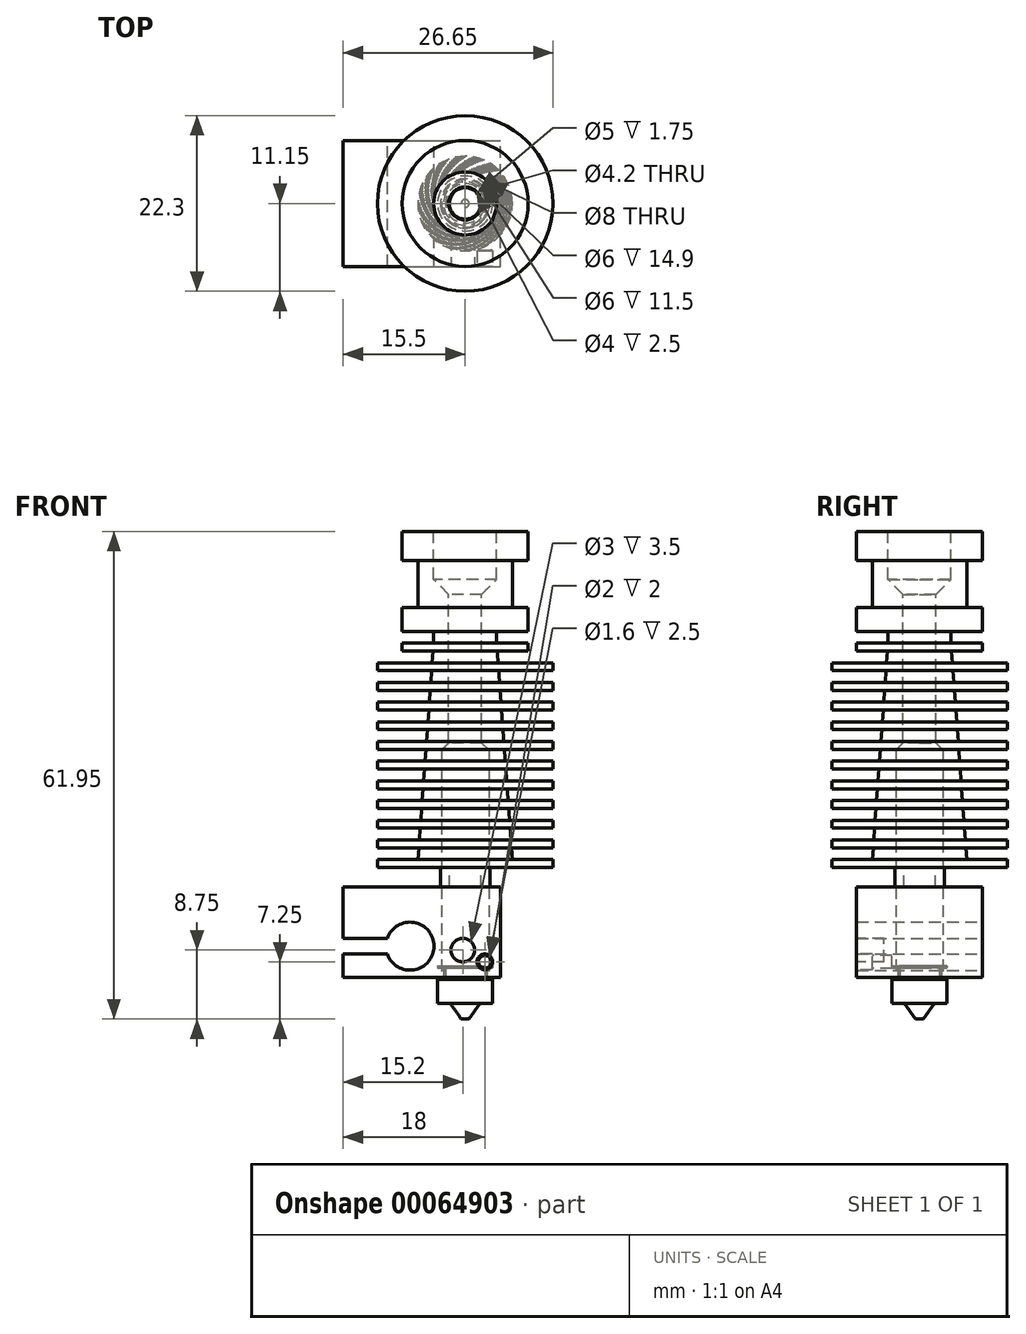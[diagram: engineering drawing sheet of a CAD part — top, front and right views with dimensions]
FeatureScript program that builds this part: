
annotation { "Feature Type Name" : "Feature", "Feature Type Description" : "" }
export const myFeature = defineFeature(function(context is Context, id is Id, definition is map)
    precondition{}
    {
        {
            var Q0;
            Q0=qCreatedBy(makeId("Top.planeOp"),FACE);
            var sketch = newSketch(context, id + "F0", { "sketchPlane" : qUnion([Q0])});
            skCircle(sketch, "E0", {"center": v(0, 0) * mm, "radius": 8 * mm});
            skSolve(sketch);
        }
        {
            var Q0;
            Q0=makeQuery(id+"F0.imprint","IMPRINT",FACE,{"disambiguationData":[TD([[makeQuery(id+"F0.imprint","IMPRINT",EDGE,{"derivedFrom":sQuery(id+"F0.wireOp",EDGE,"E0")}),1.0]])]});
            var Q1;
            Q1=sQuery(id+"F0.wireOp",EDGE,"E0");
            extrude(context, id + "F1", {"entities" : qUnion([Q0]), "surfaceEntities" : qUnion([Q1]), "oppositeDirection" : true, "depth" : 3.7 * mm});
        }
        {
            var Q0;
            Q0=makeQuery(id+"F1.opExtrude","CAP_FACE",FACE,{"disambiguationData":[OSD([sQuery(id+"F0.wireOp",EDGE,"E0")])],"isStart":false});
            var sketch = newSketch(context, id + "F2", { "sketchPlane" : qUnion([Q0])});
            skCircle(sketch, "E1", {"center": v(0, 0) * mm, "radius": 6 * mm});
            skSolve(sketch);
        }
        {
            var Q0;
            Q0=makeQuery(id+"F2.imprint","IMPRINT",FACE,{"disambiguationData":[TD([[makeQuery(id+"F2.imprint","IMPRINT",EDGE,{"derivedFrom":sQuery(id+"F2.wireOp",EDGE,"E1")}),1.0]])]});
            var Q1;
            Q1=sQuery(id+"F2.wireOp",EDGE,"E1");
            extrude(context, id + "F3", {"entities" : qUnion([Q0]), "operationType" : NewBodyOperationType.ADD, "surfaceEntities" : qUnion([Q1]), "depth" : 6 * mm});
        }
        {
            var Q0;
            Q0=makeQuery(id+"F3.opExtrude","CAP_FACE",FACE,{"disambiguationData":[OSD([sQuery(id+"F2.wireOp",EDGE,"E1")])],"isStart":false});
            var sketch = newSketch(context, id + "F4", { "sketchPlane" : qUnion([Q0])});
            skCircle(sketch, "E2", {"center": v(0, 0) * mm, "radius": 8 * mm});
            skSolve(sketch);
        }
        {
            var Q0;
            Q0=qSketchRegion(id+"F4",true);
            extrude(context, id + "F5", {"entities" : qUnion([Q0]), "operationType" : NewBodyOperationType.ADD, "depth" : 3 * mm});
        }
        {
            var Q0;
            Q0=qCreatedBy(makeId("Front.planeOp"),FACE);
            var sketch = newSketch(context, id + "F6", { "sketchPlane" : qUnion([Q0])});
            skLineSegment(sketch, "E3", {"start": v(0, 0) * mm, "end": v(0, -12.7) * mm});
            skLineSegment(sketch, "E4.bottom", {"start": v(0, -12.7) * mm, "end": v(4, -12.7) * mm});
            skLineSegment(sketch, "E4.top", {"start": v(0, -14.2) * mm, "end": v(4, -14.2) * mm});
            skLineSegment(sketch, "E4.left", {"start": v(0, -12.7) * mm, "end": v(0, -14.2) * mm});
            skLineSegment(sketch, "E4.right", {"start": v(4, -12.7) * mm, "end": v(4, -14.2) * mm});
            skLineSegment(sketch, "E5.bottom", {"start": v(0, -14.2) * mm, "end": v(8, -14.2) * mm});
            skLineSegment(sketch, "E5.top", {"start": v(0, -15.2) * mm, "end": v(8, -15.2) * mm});
            skLineSegment(sketch, "E5.left", {"start": v(0, -14.2) * mm, "end": v(0, -15.2) * mm});
            skLineSegment(sketch, "E5.right", {"start": v(8, -14.2) * mm, "end": v(8, -15.2) * mm});
            skLineSegment(sketch, "E6", {"start": v(0, -15.2) * mm, "end": v(0, -16.7) * mm});
            skLineSegment(sketch, "E7.bottom", {"start": v(0, -16.7) * mm, "end": v(11.15, -16.7) * mm});
            skLineSegment(sketch, "E7.top", {"start": v(0, -17.7) * mm, "end": v(11.15, -17.7) * mm});
            skLineSegment(sketch, "E7.left", {"start": v(0, -16.7) * mm, "end": v(0, -17.7) * mm});
            skLineSegment(sketch, "E7.right", {"start": v(11.15, -16.7) * mm, "end": v(11.15, -17.7) * mm});
            skLineSegment(sketch, "E8.1.0.0", {"start": v(0, -20.2) * mm, "end": v(11.15, -20.2) * mm});
            skLineSegment(sketch, "E8.1.0.1", {"start": v(0, -19.2) * mm, "end": v(11.15, -19.2) * mm});
            skLineSegment(sketch, "E8.1.0.2", {"start": v(0, -19.2) * mm, "end": v(0, -20.2) * mm});
            skLineSegment(sketch, "E8.1.0.3", {"start": v(11.15, -19.2) * mm, "end": v(11.15, -20.2) * mm});
            skLineSegment(sketch, "E8.2.0.0", {"start": v(0, -22.7) * mm, "end": v(11.15, -22.7) * mm});
            skLineSegment(sketch, "E8.2.0.1", {"start": v(0, -21.7) * mm, "end": v(11.15, -21.7) * mm});
            skLineSegment(sketch, "E8.2.0.2", {"start": v(0, -21.7) * mm, "end": v(0, -22.7) * mm});
            skLineSegment(sketch, "E8.2.0.3", {"start": v(11.15, -21.7) * mm, "end": v(11.15, -22.7) * mm});
            skLineSegment(sketch, "E8.3.0.0", {"start": v(0, -25.2) * mm, "end": v(11.15, -25.2) * mm});
            skLineSegment(sketch, "E8.3.0.1", {"start": v(0, -24.2) * mm, "end": v(11.15, -24.2) * mm});
            skLineSegment(sketch, "E8.3.0.2", {"start": v(0, -24.2) * mm, "end": v(0, -25.2) * mm});
            skLineSegment(sketch, "E8.3.0.3", {"start": v(11.15, -24.2) * mm, "end": v(11.15, -25.2) * mm});
            skLineSegment(sketch, "E8.4.0.0", {"start": v(0, -27.7) * mm, "end": v(11.15, -27.7) * mm});
            skLineSegment(sketch, "E8.4.0.1", {"start": v(0, -26.7) * mm, "end": v(11.15, -26.7) * mm});
            skLineSegment(sketch, "E8.4.0.2", {"start": v(0, -26.7) * mm, "end": v(0, -27.7) * mm});
            skLineSegment(sketch, "E8.4.0.3", {"start": v(11.15, -26.7) * mm, "end": v(11.15, -27.7) * mm});
            skLineSegment(sketch, "E8.5.0.0", {"start": v(0, -30.2) * mm, "end": v(11.15, -30.2) * mm});
            skLineSegment(sketch, "E8.5.0.1", {"start": v(0, -29.2) * mm, "end": v(11.15, -29.2) * mm});
            skLineSegment(sketch, "E8.5.0.2", {"start": v(0, -29.2) * mm, "end": v(0, -30.2) * mm});
            skLineSegment(sketch, "E8.5.0.3", {"start": v(11.15, -29.2) * mm, "end": v(11.15, -30.2) * mm});
            skLineSegment(sketch, "E8.6.0.0", {"start": v(0, -32.7) * mm, "end": v(11.15, -32.7) * mm});
            skLineSegment(sketch, "E8.6.0.1", {"start": v(0, -31.7) * mm, "end": v(11.15, -31.7) * mm});
            skLineSegment(sketch, "E8.6.0.2", {"start": v(0, -31.7) * mm, "end": v(0, -32.7) * mm});
            skLineSegment(sketch, "E8.6.0.3", {"start": v(11.15, -31.7) * mm, "end": v(11.15, -32.7) * mm});
            skLineSegment(sketch, "E8.7.0.0", {"start": v(0, -35.2) * mm, "end": v(11.15, -35.2) * mm});
            skLineSegment(sketch, "E8.7.0.1", {"start": v(0, -34.2) * mm, "end": v(11.15, -34.2) * mm});
            skLineSegment(sketch, "E8.7.0.2", {"start": v(0, -34.2) * mm, "end": v(0, -35.2) * mm});
            skLineSegment(sketch, "E8.7.0.3", {"start": v(11.15, -34.2) * mm, "end": v(11.15, -35.2) * mm});
            skLineSegment(sketch, "E8.8.0.0", {"start": v(0, -37.7) * mm, "end": v(11.15, -37.7) * mm});
            skLineSegment(sketch, "E8.8.0.1", {"start": v(0, -36.7) * mm, "end": v(11.15, -36.7) * mm});
            skLineSegment(sketch, "E8.8.0.2", {"start": v(0, -36.7) * mm, "end": v(0, -37.7) * mm});
            skLineSegment(sketch, "E8.8.0.3", {"start": v(11.15, -36.7) * mm, "end": v(11.15, -37.7) * mm});
            skLineSegment(sketch, "E8.9.0.0", {"start": v(0, -40.2) * mm, "end": v(11.15, -40.2) * mm});
            skLineSegment(sketch, "E8.9.0.1", {"start": v(0, -39.2) * mm, "end": v(11.15, -39.2) * mm});
            skLineSegment(sketch, "E8.9.0.2", {"start": v(0, -39.2) * mm, "end": v(0, -40.2) * mm});
            skLineSegment(sketch, "E8.9.0.3", {"start": v(11.15, -39.2) * mm, "end": v(11.15, -40.2) * mm});
            skLineSegment(sketch, "E8.10.0.0", {"start": v(0, -42.7) * mm, "end": v(11.15, -42.7) * mm});
            skLineSegment(sketch, "E8.10.0.1", {"start": v(0, -41.7) * mm, "end": v(11.15, -41.7) * mm});
            skLineSegment(sketch, "E8.10.0.2", {"start": v(0, -41.7) * mm, "end": v(0, -42.7) * mm});
            skLineSegment(sketch, "E8.10.0.3", {"start": v(11.15, -41.7) * mm, "end": v(11.15, -42.7) * mm});
            skLineSegment(sketch, "E8.direction1", {"start": v(0, -17.7) * mm, "end": v(0, -20.2) * mm, "construction": true});
            skLineSegment(sketch, "E9", {"start": v(0, -41.7) * mm, "end": v(6, -41.7) * mm});
            skLineSegment(sketch, "E10", {"start": v(4.07, -15.2) * mm, "end": v(4.18, -16.7) * mm});
            skLineSegment(sketch, "E11.trimOffspring", {"start": v(4.25, -17.7) * mm, "end": v(4.36, -19.2) * mm});
            skLineSegment(sketch, "E12.trimOffspring", {"start": v(4.44, -20.2) * mm, "end": v(4.55, -21.7) * mm});
            skLineSegment(sketch, "E13.trimOffspring", {"start": v(4.62, -22.7) * mm, "end": v(4.73, -24.2) * mm});
            skLineSegment(sketch, "E14.trimOffspring", {"start": v(4.8, -25.2) * mm, "end": v(4.9, -26.7) * mm});
            skLineSegment(sketch, "E15.trimOffspring", {"start": v(4.98, -27.7) * mm, "end": v(5.1, -29.2) * mm});
            skLineSegment(sketch, "E16.trimOffspring", {"start": v(5.16, -30.2) * mm, "end": v(5.27, -31.7) * mm});
            skLineSegment(sketch, "E17.trimOffspring", {"start": v(5.35, -32.7) * mm, "end": v(5.45, -34.2) * mm});
            skLineSegment(sketch, "E18.trimOffspring", {"start": v(5.53, -35.2) * mm, "end": v(5.64, -36.7) * mm});
            skLineSegment(sketch, "E19.trimOffspring", {"start": v(5.7, -37.7) * mm, "end": v(5.82, -39.2) * mm});
            skLineSegment(sketch, "E20.trimOffspring", {"start": v(5.9, -40.2) * mm, "end": v(6, -41.7) * mm});
            skLineSegment(sketch, "E21", {"start": v(0, -17.7) * mm, "end": v(0, -19.2) * mm});
            skLineSegment(sketch, "E22", {"start": v(0, -20.2) * mm, "end": v(0, -21.7) * mm});
            skLineSegment(sketch, "E23", {"start": v(0, -22.7) * mm, "end": v(0, -24.2) * mm});
            skLineSegment(sketch, "E24", {"start": v(0, -25.2) * mm, "end": v(0, -26.7) * mm});
            skLineSegment(sketch, "E25", {"start": v(0, -27.7) * mm, "end": v(0, -29.2) * mm});
            skLineSegment(sketch, "E26", {"start": v(0, -30.2) * mm, "end": v(0, -31.7) * mm});
            skLineSegment(sketch, "E27", {"start": v(0, -32.7) * mm, "end": v(0, -34.2) * mm});
            skLineSegment(sketch, "E28", {"start": v(0, -35.2) * mm, "end": v(0, -36.7) * mm});
            skLineSegment(sketch, "E29", {"start": v(0, -37.7) * mm, "end": v(0, -39.2) * mm});
            skLineSegment(sketch, "E30", {"start": v(0, -40.2) * mm, "end": v(0, -41.7) * mm});
            skLineSegment(sketch, "E31.right", {"start": v(3, -42.7) * mm, "end": v(3, -45.2) * mm});
            skLineSegment(sketch, "E32", {"start": v(3, -45.2) * mm, "end": v(2, -45.2) * mm});
            skLineSegment(sketch, "E33", {"start": v(2, -45.2) * mm, "end": v(2, -42.7) * mm});
            skLineSegment(sketch, "E34.bottom", {"start": v(2, -45.2) * mm, "end": v(3, -45.2) * mm});
            skLineSegment(sketch, "E34.top", {"start": v(2, -47.3) * mm, "end": v(3, -47.3) * mm});
            skLineSegment(sketch, "E34.left", {"start": v(2, -45.2) * mm, "end": v(2, -47.3) * mm});
            skLineSegment(sketch, "E34.right", {"start": v(3, -45.2) * mm, "end": v(3, -47.3) * mm});
            skLineSegment(sketch, "E35.bottom", {"start": v(3, -47.3) * mm, "end": v(3.75, -47.3) * mm});
            skLineSegment(sketch, "E35.top", {"start": v(3, -46.56) * mm, "end": v(3.75, -46.56) * mm});
            skLineSegment(sketch, "E35.left", {"start": v(3, -47.3) * mm, "end": v(3, -46.56) * mm});
            skLineSegment(sketch, "E35.right", {"start": v(3.75, -47.3) * mm, "end": v(3.75, -46.56) * mm});
            skLineSegment(sketch, "E36.bottom", {"start": v(2, -42.7) * mm, "end": v(3, -42.7) * mm});
            skLineSegment(sketch, "E36.top", {"start": v(2, -41.7) * mm, "end": v(3, -41.7) * mm});
            skLineSegment(sketch, "E36.left", {"start": v(2, -42.7) * mm, "end": v(2, -41.7) * mm});
            skLineSegment(sketch, "E36.right", {"start": v(3, -42.7) * mm, "end": v(3, -41.7) * mm});
            skSolve(sketch);
        }
        {
            var Q0;
            Q0=qSketchRegion(id+"F6",true);
            var Q1;
            {var subQ0=sQuery(id+"F6.wireOp",EDGE,"E31.right");Q1=makeQuery(id+"F6.imprint","IMPRINT",FACE,{"disambiguationData":[TD([[makeQuery(id+"F6.imprint","IMPRINT",EDGE,{"derivedFrom":subQ0}),-1.0]])]});}
            var Q2;
            Q2=makeQuery(id+"F6.imprint","IMPRINT",FACE,{"disambiguationData":[TD([[makeQuery(id+"F6.imprint","IMPRINT",EDGE,{"derivedFrom":sQuery(id+"F6.wireOp",EDGE,"E34.bottom")}),-1.0]])]});
            var Q3;
            Q3=makeQuery(id+"F6.imprint","IMPRINT",FACE,{"disambiguationData":[TD([[makeQuery(id+"F6.imprint","IMPRINT",EDGE,{"derivedFrom":sQuery(id+"F6.wireOp",EDGE,"E36.bottom")}),1.0]])]});
            var Q4;
            Q4=makeQuery(id+"F6.imprint","IMPRINT",FACE,{"disambiguationData":[TD([[makeQuery(id+"F6.imprint","IMPRINT",EDGE,{"derivedFrom":sQuery(id+"F6.wireOp",EDGE,"E31.right")}),-1.0]])]});
            var Q5;
            Q5=makeQuery(id+"F6.imprint","IMPRINT",FACE,{"disambiguationData":[TD([[makeQuery(id+"F6.imprint","IMPRINT",EDGE,{"derivedFrom":sQuery(id+"F6.wireOp",EDGE,"E34.bottom")}),-1.0]])]});
            var Q6;
            Q6=sQuery(id+"F6.wireOp",EDGE,"E3");
            revolve(context, id + "F7", {"operationType" : NewBodyOperationType.ADD, "entities" : qUnion([Q0, Q1, Q2, Q3, Q4, Q5]), "axis" : qUnion([Q6]), "revolveType" : RevolveType.FULL});
        }
        {
            var Q0;
            Q0=makeQuery(id+"F1.opExtrude","CAP_FACE",FACE,{"disambiguationData":[OSD([sQuery(id+"F0.wireOp",EDGE,"E0")])],"isStart":true});
            var sketch = newSketch(context, id + "F8", { "sketchPlane" : qUnion([Q0])});
            skCircle(sketch, "E37", {"center": v(0, 0) * mm, "radius": 2.1 * mm});
            skSolve(sketch);
        }
        {
            var Q0;
            Q0=qSketchRegion(id+"F8",true);
            extrude(context, id + "F9", {"entities" : qUnion([Q0]), "operationType" : NewBodyOperationType.REMOVE, "oppositeDirection" : true, "depth" : 42.7 * mm});
        }
        {
            var Q0;
            Q0=makeQuery(id+"F1.opExtrude","CAP_FACE",FACE,{"disambiguationData":[OSD([sQuery(id+"F0.wireOp",EDGE,"E0")])],"isStart":true});
            var sketch = newSketch(context, id + "F10", { "sketchPlane" : qUnion([Q0])});
            skCircle(sketch, "E38", {"center": v(0, 0) * mm, "radius": 4 * mm});
            skSolve(sketch);
        }
        {
            var Q0;
            Q0=qSketchRegion(id+"F10",true);
            extrude(context, id + "F11", {"entities" : qUnion([Q0]), "operationType" : NewBodyOperationType.REMOVE, "oppositeDirection" : true, "depth" : 6 * mm});
        }
        {
            var Q0;
            Q0=makeQuery(id+"F11.boolean.opBoolean","INTERSECT",EDGE,{"derivedFrom":[makeQuery(id+"F9.boolean.opBoolean","COPY",FACE,{"derivedFrom":makeQuery(id+"F9.opExtrude","SWEPT_FACE",FACE,{"disambiguationData":[OSD([sQuery(id+"F8.wireOp",EDGE,"E37")])]})}),makeQuery(id+"F11.opExtrude","CAP_FACE",FACE,{"disambiguationData":[OSD([sQuery(id+"F10.wireOp",EDGE,"E38")])],"isStart":false})]});
            chamfer(context, id + "F12", {"entities" : qUnion([Q0]), "width" : 2 * mm, "tangentPropagation" : true});
        }
        {
            var Q0;
            Q0=makeQuery(id+"F7.opRevolve","SWEPT_FACE",FACE,{"disambiguationData":[OSD([sQuery(id+"F6.wireOp",EDGE,"E8.10.0.0")])]});
            var sketch = newSketch(context, id + "F13", { "sketchPlane" : qUnion([Q0])});
            skCircle(sketch, "E39", {"center": v(0, 0) * mm, "radius": 3 * mm});
            skSolve(sketch);
        }
        {
            var Q0;
            Q0=qSketchRegion(id+"F13",true);
            extrude(context, id + "F14", {"entities" : qUnion([Q0]), "operationType" : NewBodyOperationType.REMOVE, "oppositeDirection" : true, "depth" : 14.8 * mm});
        }
        {
            var Q0;
            Q0=makeQuery(id+"F14.boolean.opBoolean","INTERSECT",EDGE,{"derivedFrom":[makeQuery(id+"F9.boolean.opBoolean","COPY",FACE,{"derivedFrom":makeQuery(id+"F9.opExtrude","SWEPT_FACE",FACE,{"disambiguationData":[OSD([sQuery(id+"F8.wireOp",EDGE,"E37")])]})}),makeQuery(id+"F14.opExtrude","CAP_FACE",FACE,{"disambiguationData":[OSD([sQuery(id+"F13.wireOp",EDGE,"E39")])],"isStart":false})]});
            chamfer(context, id + "F15", {"entities" : qUnion([Q0]), "width" : 1 * mm, "tangentPropagation" : true});
        }
        {
            var Q0;
            Q0=qCreatedBy(makeId("Front.planeOp"),FACE);
            var sketch = newSketch(context, id + "F16", { "sketchPlane" : qUnion([Q0])});
            skLineSegment(sketch, "E40.bottom", {"start": v(-15.5, -45.2) * mm, "end": v(4.5, -45.2) * mm});
            skLineSegment(sketch, "E40.top", {"start": v(-15.5, -56.7) * mm, "end": v(4.5, -56.7) * mm});
            skLineSegment(sketch, "E40.left", {"start": v(-15.5, -45.2) * mm, "end": v(-15.5, -51.7) * mm});
            skLineSegment(sketch, "E40.right", {"start": v(4.5, -45.2) * mm, "end": v(4.5, -56.7) * mm});
            skArc(sketch, "E41", {"start": v(-9.88, -53.7) * mm, "mid": v(-3.95, -52.7) * mm, "end": v(-9.88, -51.7) * mm});
            skLineSegment(sketch, "E42.top", {"start": v(-15.5, -51.7) * mm, "end": v(-9.88, -51.7) * mm});
            skLineSegment(sketch, "E43.top", {"start": v(-15.5, -53.7) * mm, "end": v(-9.88, -53.7) * mm});
            skLineSegment(sketch, "E44.trimOffspring", {"start": v(-15.5, -53.7) * mm, "end": v(-15.5, -56.7) * mm});
            skSolve(sketch);
        }
        {
            var Q0;
            Q0=makeQuery(id+"F16.imprint","IMPRINT",FACE,{"disambiguationData":[TD([[makeQuery(id+"F16.imprint","IMPRINT",EDGE,{"derivedFrom":sQuery(id+"F16.wireOp",EDGE,"E40.bottom")}),-1.0]])]});
            var Q1;
            Q1=makeQuery(id+"F16.imprint","IMPRINT",FACE,{"disambiguationData":[TD([[makeQuery(id+"F16.imprint","IMPRINT",EDGE,{"derivedFrom":sQuery(id+"F16.wireOp",EDGE,"hSTLO5rz-Z077-ZaO5-nEVS-phWlFBx8dYmu")}),1.0]])]});
            var Q2;
            Q2=makeQuery(id+"F16.imprint","IMPRINT",FACE,{"disambiguationData":[TD([[makeQuery(id+"F16.imprint","IMPRINT",EDGE,{"derivedFrom":sQuery(id+"F16.wireOp",EDGE,"1ucrc5hz-Jwvr-DOmE-K7qY-mdj6J8iSEPF0")}),1.0]])]});
            extrude(context, id + "F17", {"entities" : qUnion([Q0, Q1, Q2]), "depth" : 16 * mm, "symmetric" : true});
        }
        {
            var Q0;
            Q0=makeQuery(id+"F17.opExtrude","SWEPT_FACE",FACE,{"disambiguationData":[OSD([sQuery(id+"F16.wireOp",EDGE,"E40.top")])]});
            var sketch = newSketch(context, id + "F18", { "sketchPlane" : qUnion([Q0])});
            skCircle(sketch, "E45", {"center": v(0, 0) * mm, "radius": 3 * mm});
            skSolve(sketch);
        }
        {
            var Q0;
            Q0=qSketchRegion(id+"F18",true);
            extrude(context, id + "F19", {"entities" : qUnion([Q0]), "operationType" : NewBodyOperationType.REMOVE, "oppositeDirection" : true, "depth" : 11.5 * mm});
        }
        {
            var Q0;
            Q0=qCreatedBy(makeId("Front.planeOp"),FACE);
            var sketch = newSketch(context, id + "F20", { "sketchPlane" : qUnion([Q0])});
            skLineSegment(sketch, "E46.bottom", {"start": v(0, -56.95) * mm, "end": v(3.5, -56.95) * mm});
            skLineSegment(sketch, "E46.right", {"start": v(3.5, -56.95) * mm, "end": v(3.5, -59.95) * mm});
            skLineSegment(sketch, "E47.top", {"start": v(0, -61.95) * mm, "end": v(0.5, -61.95) * mm});
            skLineSegment(sketch, "E48", {"start": v(0.5, -61.95) * mm, "end": v(1.9, -59.95) * mm});
            skLineSegment(sketch, "E49.trimOffspring", {"start": v(1.9, -59.95) * mm, "end": v(3.5, -59.95) * mm});
            skLineSegment(sketch, "E50", {"start": v(0, -61.95) * mm, "end": v(0, -56.95) * mm});
            skLineSegment(sketch, "E51", {"start": v(0, -56.95) * mm, "end": v(2.5, -56.95) * mm});
            skLineSegment(sketch, "E52", {"start": v(2.5, -56.95) * mm, "end": v(2.5, -55.45) * mm});
            skLineSegment(sketch, "E53", {"start": v(2.5, -55.45) * mm, "end": v(2.75, -55.45) * mm});
            skLineSegment(sketch, "E54", {"start": v(2.75, -55.45) * mm, "end": v(2.75, -56.95) * mm});
            skLineSegment(sketch, "E55.bottom", {"start": v(2.5, -55.45) * mm, "end": v(3.5, -55.45) * mm});
            skLineSegment(sketch, "E55.top", {"start": v(2.5, -55.2) * mm, "end": v(3.5, -55.2) * mm});
            skLineSegment(sketch, "E55.left", {"start": v(2.5, -55.45) * mm, "end": v(2.5, -55.2) * mm});
            skLineSegment(sketch, "E55.right", {"start": v(3.5, -55.45) * mm, "end": v(3.5, -55.2) * mm});
            skSolve(sketch);
        }
        {
            var Q0;
            Q0=qSketchRegion(id+"F20",true);
            var Q1;
            Q1=sQuery(id+"F20.wireOp",EDGE,"E50");
            revolve(context, id + "F21", {"entities" : qUnion([Q0]), "axis" : qUnion([Q1]), "revolveType" : RevolveType.FULL});
        }
        {
            var Q0;
            Q0=makeQuery(id+"F17.opExtrude","CAP_FACE",FACE,{"disambiguationData":[OSD([sQuery(id+"F16.wireOp",EDGE,"E40.bottom"),sQuery(id+"F16.wireOp",EDGE,"E40.top"),sQuery(id+"F16.wireOp",EDGE,"E40.left"),sQuery(id+"F16.wireOp",EDGE,"E40.right"),sQuery(id+"F16.wireOp",EDGE,"E41"),sQuery(id+"F16.wireOp",EDGE,"E42.top"),sQuery(id+"F16.wireOp",EDGE,"E43.top"),sQuery(id+"F16.wireOp",EDGE,"E44.trimOffspring")])],"isStart":false});
            var sketch = newSketch(context, id + "F22", { "sketchPlane" : qUnion([Q0])});
            skCircle(sketch, "E56", {"center": v(-0.3, -53.2) * mm, "radius": 1.5 * mm});
            skCircle(sketch, "E57", {"center": v(2.5, -54.7) * mm, "radius": 1 * mm});
            skCircle(sketch, "E58", {"center": v(2.5, -54.7) * mm, "radius": 0.8 * mm});
            skSolve(sketch);
        }
        {
            var Q0;
            Q0=makeQuery(id+"F22.imprint","IMPRINT",FACE,{"disambiguationData":[TD([[makeQuery(id+"F22.imprint","IMPRINT",EDGE,{"derivedFrom":sQuery(id+"F22.wireOp",EDGE,"E56")}),1.0]])]});
            extrude(context, id + "F23", {"entities" : qUnion([Q0]), "operationType" : NewBodyOperationType.REMOVE, "oppositeDirection" : true, "depth" : 3.5 * mm});
        }
        {
            var Q0;
            Q0=makeQuery(id+"F22.imprint","IMPRINT",FACE,{"disambiguationData":[TD([[makeQuery(id+"F22.imprint","IMPRINT",EDGE,{"derivedFrom":sQuery(id+"F22.wireOp",EDGE,"E57")}),1.0]])]});
            extrude(context, id + "F24", {"entities" : qUnion([Q0]), "operationType" : NewBodyOperationType.REMOVE, "oppositeDirection" : true, "depth" : 2 * mm});
        }
        {
            var Q0;
            Q0=makeQuery(id+"F22.imprint","IMPRINT",FACE,{"disambiguationData":[TD([[makeQuery(id+"F22.imprint","IMPRINT",EDGE,{"derivedFrom":sQuery(id+"F22.wireOp",EDGE,"E58")}),1.0]])]});
            extrude(context, id + "F25", {"entities" : qUnion([Q0]), "operationType" : NewBodyOperationType.REMOVE, "oppositeDirection" : true, "depth" : 4.5 * mm});
        }
        {
            var Q0;
            {var subQ0=sQuery(id+"F6.wireOp",EDGE,"E8.10.0.0");Q0=makeQuery(id+"F7.opRevolve","SWEPT_FACE",FACE,{"disambiguationData":[OSD([subQ0]),TDD([makeQuery(id+"F6.imprint","IMPRINT",EDGE,{"disambiguationData":[TD([[makeQuery(id+"F6.imprint","INTERSECT",VERTEX,{"derivedFrom":[subQ0,sQuery(id+"F6.wireOp",EDGE,"E8.10.0.3")]}),1.0]])],"derivedFrom":subQ0})])]});}
            var sketch = newSketch(context, id + "F26", { "sketchPlane" : qUnion([Q0])});
            skCircle(sketch, "E59", {"center": v(0, 0) * mm, "radius": 3.12 * mm});
            skSolve(sketch);
        }
        {
            var Q0;
            Q0=makeQuery(id+"F26.imprint","IMPRINT",FACE,{"disambiguationData":[TD([[makeQuery(id+"F26.imprint","IMPRINT",EDGE,{"derivedFrom":sQuery(id+"F26.wireOp",EDGE,"E59")}),1.0]])]});
            extrude(context, id + "F27", {"entities" : qUnion([Q0]), "operationType" : NewBodyOperationType.ADD, "depth" : 5 * mm});
        }
    });
